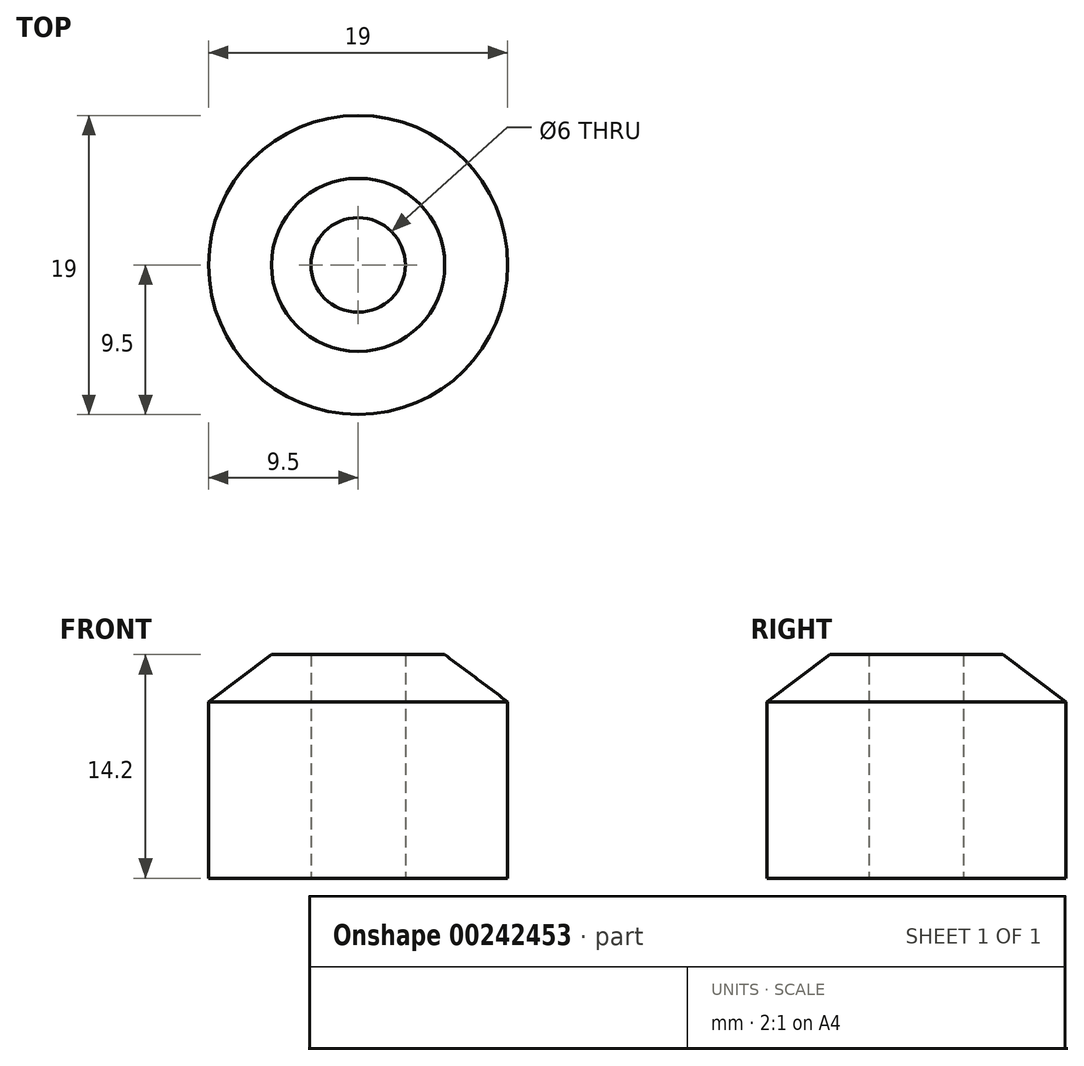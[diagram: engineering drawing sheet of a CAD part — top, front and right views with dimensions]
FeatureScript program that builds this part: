
annotation { "Feature Type Name" : "Feature", "Feature Type Description" : "" }
export const myFeature = defineFeature(function(context is Context, id is Id, definition is map)
    precondition{}
    {
        {
            var Q0;
            Q0=qCreatedBy(makeId("Top.planeOp"),FACE);
            var sketch = newSketch(context, id + "F0", { "sketchPlane" : qUnion([Q0])});
            skCircle(sketch, "E0", {"center": v(0, 0) * mm, "radius": 3 * mm});
            skCircle(sketch, "E1", {"center": v(0, 0) * mm, "radius": 9.5 * mm});
            skSolve(sketch);
        }
        {
            var Q0;
            Q0=makeQuery(id+"F0.imprint","IMPRINT",FACE,{"disambiguationData":[TD([[makeQuery(id+"F0.imprint","IMPRINT",EDGE,{"derivedFrom":sQuery(id+"F0.wireOp",EDGE,"E0")}),-1.0]])]});
            extrude(context, id + "F1", {"entities" : qUnion([Q0]), "depth" : 14.2 * mm, "offsetDistance" : 25 * mm});
        }
        {
            var Q0;
            Q0=makeQuery(id+"F1.opExtrude","CAP_EDGE",EDGE,{"disambiguationData":[OSD([sQuery(id+"F0.wireOp",EDGE,"E1")])],"isStart":false});
            chamfer(context, id + "F2", {"entities" : qUnion([Q0]), "chamferType" : ChamferType.TWO_OFFSETS, "width1" : 4 * mm, "oppositeDirection" : false, "width2" : 3 * mm, "tangentPropagation" : true});
        }
    });
